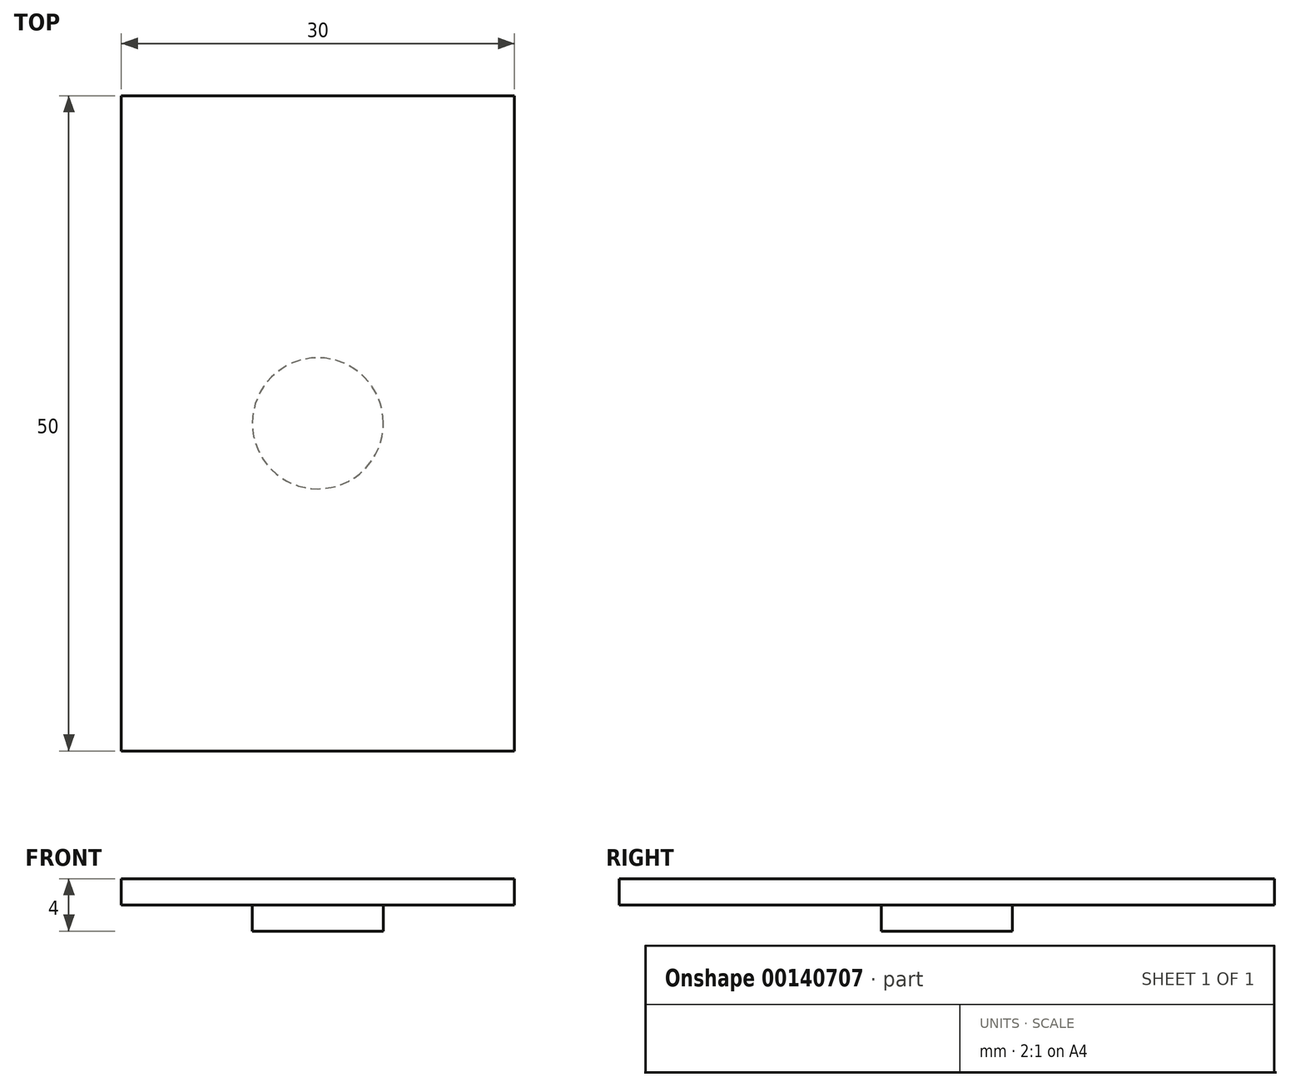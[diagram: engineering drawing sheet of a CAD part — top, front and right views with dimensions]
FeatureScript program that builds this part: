
annotation { "Feature Type Name" : "Feature", "Feature Type Description" : "" }
export const myFeature = defineFeature(function(context is Context, id is Id, definition is map)
    precondition{}
    {
        {
            var Q0;
            Q0=qCreatedBy(makeId("Top.planeOp"),FACE);
            var sketch = newSketch(context, id + "F0", { "sketchPlane" : qUnion([Q0])});
            skCircle(sketch, "E0", {"center": v(0, 0) * mm, "radius": 5 * mm});
            skLineSegment(sketch, "E1.bottom", {"start": v(15, 25) * mm, "end": v(-15, 25) * mm});
            skLineSegment(sketch, "E1.top", {"start": v(15, -25) * mm, "end": v(-15, -25) * mm});
            skLineSegment(sketch, "E1.left", {"start": v(15, 25) * mm, "end": v(15, -25) * mm});
            skLineSegment(sketch, "E1.right", {"start": v(-15, 25) * mm, "end": v(-15, -25) * mm});
            skSolve(sketch);
        }
        {
            var Q0;
            Q0=makeQuery(id+"F0.imprint","IMPRINT",FACE,{"disambiguationData":[TD([[makeQuery(id+"F0.imprint","IMPRINT",EDGE,{"derivedFrom":sQuery(id+"F0.wireOp",EDGE,"E0")}),1.0]])]});
            var Q1;
            Q1=makeQuery(id+"F0.imprint","IMPRINT",FACE,{"disambiguationData":[TD([[makeQuery(id+"F0.imprint","IMPRINT",EDGE,{"derivedFrom":sQuery(id+"F0.wireOp",EDGE,"E0")}),-1.0]])]});
            extrude(context, id + "F1", {"entities" : qUnion([Q0, Q1]), "depth" : 2 * mm});
        }
        {
            var Q0;
            Q0=makeQuery(id+"F0.imprint","IMPRINT",FACE,{"disambiguationData":[TD([[makeQuery(id+"F0.imprint","IMPRINT",EDGE,{"derivedFrom":sQuery(id+"F0.wireOp",EDGE,"E0")}),1.0]])]});
            extrude(context, id + "F2", {"entities" : qUnion([Q0]), "operationType" : NewBodyOperationType.ADD, "oppositeDirection" : true, "depth" : 2 * mm});
        }
    });
